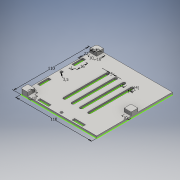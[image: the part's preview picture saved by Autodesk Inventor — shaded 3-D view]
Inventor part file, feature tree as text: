
AUTODESK INVENTOR PART (.ipt)
format: ipt  version: 2016 (Build 200138000, 138)  size: 195,072 bytes
history: native  units: mm
features: fillet x3, extrude x2, sketch x1
ambient origin geometry x8: Origin, YZ Plane, XZ Plane, XY Plane, X Axis, Y Axis, Z Axis, Center Point
bodies: Body1 (feature_tree)
feature tree (6):
  sketch  "Sketch1"  dims[d5=110.0mm d6=110.0mm d7=2.0mm d8=22.0mm d10=4.0mm d11=16.0mm d12=2.0mm d20=3.5mm d21=10.0mm d22=10.0mm d25=10.0mm d26=4.0mm d30=4.0mm d33=4.0mm d34=4.0mm d35=4.0mm d37=10.0mm d38=10.0mm d43=3.0mm d44=0.0mm d45=8.0mm d46=0.0mm d47=3.0mm d48=2.0mm d49=2.0mm]
  extrude  "Extrusion3"  Depth=110.0mm
  extrude  "Extrusion4"  Depth=2.0mm
  fillet  "Fillet1"  Radius=22.0mm
  fillet  "Fillet2"  Radius=4.0mm
  fillet  "Fillet3"  Radius=16.0mm
